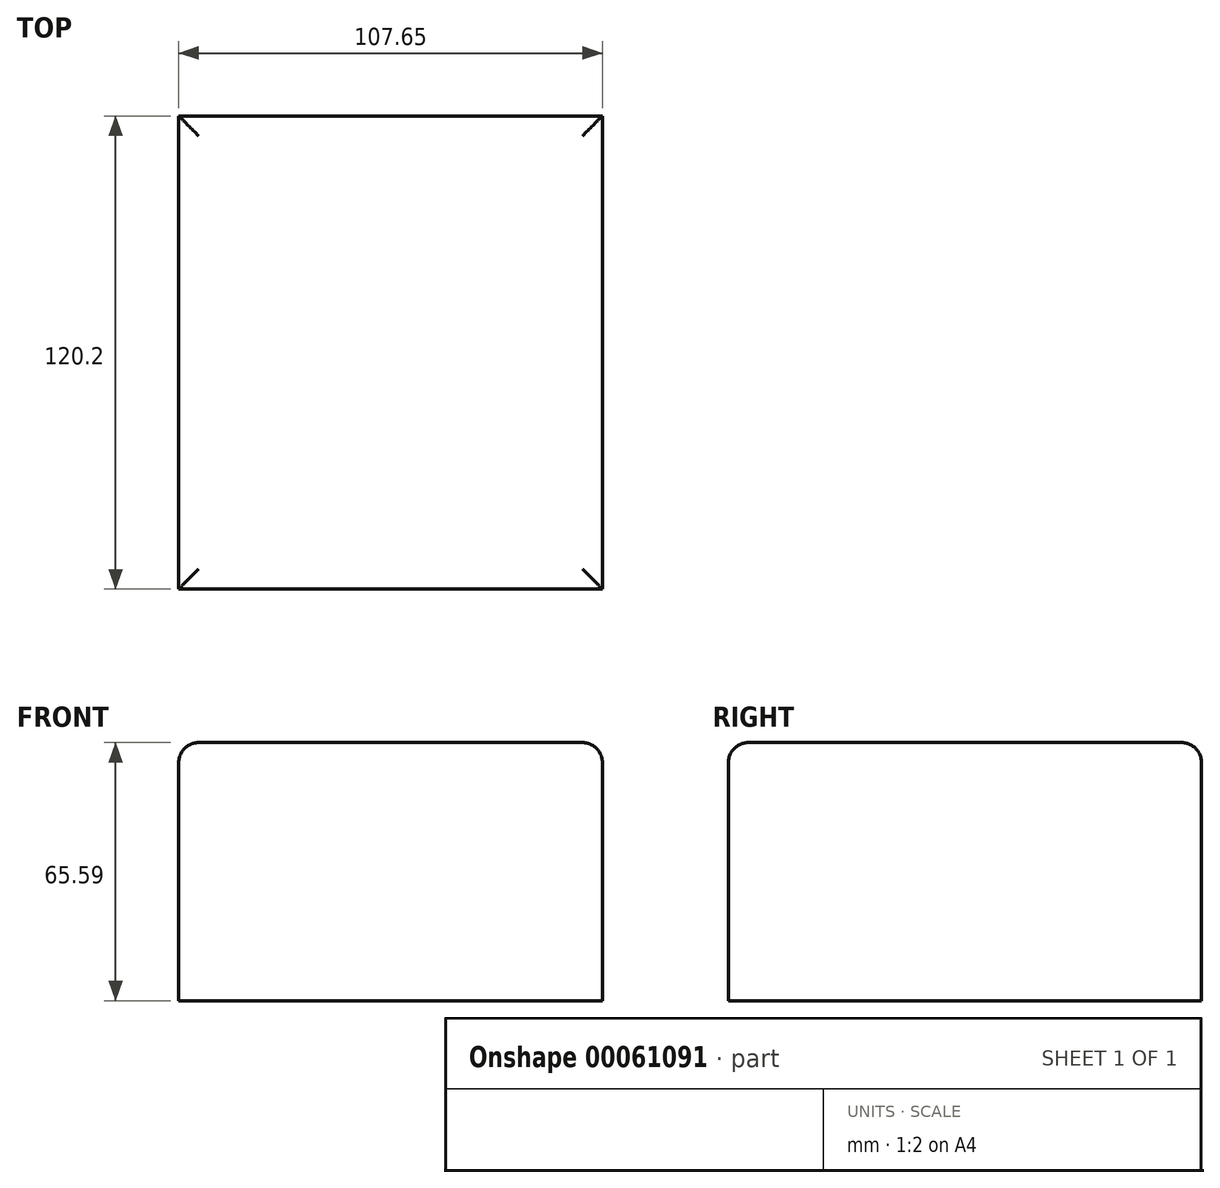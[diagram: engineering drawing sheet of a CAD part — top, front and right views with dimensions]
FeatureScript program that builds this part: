
annotation { "Feature Type Name" : "Feature", "Feature Type Description" : "" }
export const myFeature = defineFeature(function(context is Context, id is Id, definition is map)
    precondition{}
    {
        {
            var Q0;
            Q0=qCreatedBy(makeId("Front.planeOp"),FACE);
            var sketch = newSketch(context, id + "F0", { "sketchPlane" : qUnion([Q0])});
            skLineSegment(sketch, "E0.bottom", {"start": v(-65.9, 50.52) * mm, "end": v(41.74, 50.52) * mm});
            skLineSegment(sketch, "E0.top", {"start": v(-65.9, -15.07) * mm, "end": v(41.74, -15.07) * mm});
            skLineSegment(sketch, "E0.left", {"start": v(-65.9, 50.52) * mm, "end": v(-65.9, -15.07) * mm});
            skLineSegment(sketch, "E0.right", {"start": v(41.74, 50.52) * mm, "end": v(41.74, -15.07) * mm});
            skSolve(sketch);
        }
        {
            var Q0;
            Q0 = qSketchRegion(id + "F0", true);
            extrude(context, id + "F1", {"entities" : qUnion([Q0]), "depth" : 120.2 * mm});
        }
        {
            var Q0;
            Q0=makeQuery(id+"F1.opExtrude","CAP_EDGE",EDGE,{"disambiguationData":[OSD([sQuery(id+"F0.wireOp",EDGE,"E0.bottom")])],"isStart":false});
            var Q1;
            Q1=makeQuery(id+"F1.opExtrude","CAP_EDGE",EDGE,{"disambiguationData":[OSD([sQuery(id+"F0.wireOp",EDGE,"E0.bottom")])],"isStart":true});
            var Q2;
            Q2=makeQuery(id+"F1.opExtrude","SWEPT_EDGE",EDGE,{"disambiguationData":[OSD([sQuery(id+"F0.wireOp",EDGE,"E0.bottom"),sQuery(id+"F0.wireOp",EDGE,"E0.right")])]});
            var Q3;
            Q3=makeQuery(id+"F1.opExtrude","SWEPT_EDGE",EDGE,{"disambiguationData":[OSD([sQuery(id+"F0.wireOp",EDGE,"E0.bottom"),sQuery(id+"F0.wireOp",EDGE,"E0.left")])]});
            fillet(context, id + "F2", {"entities" : qUnion([Q0, Q1, Q2, Q3]), "radius" : 5.08 * mm, "tangentPropagation" : true, "allowEdgeOverflow" : false});
        }
    });
